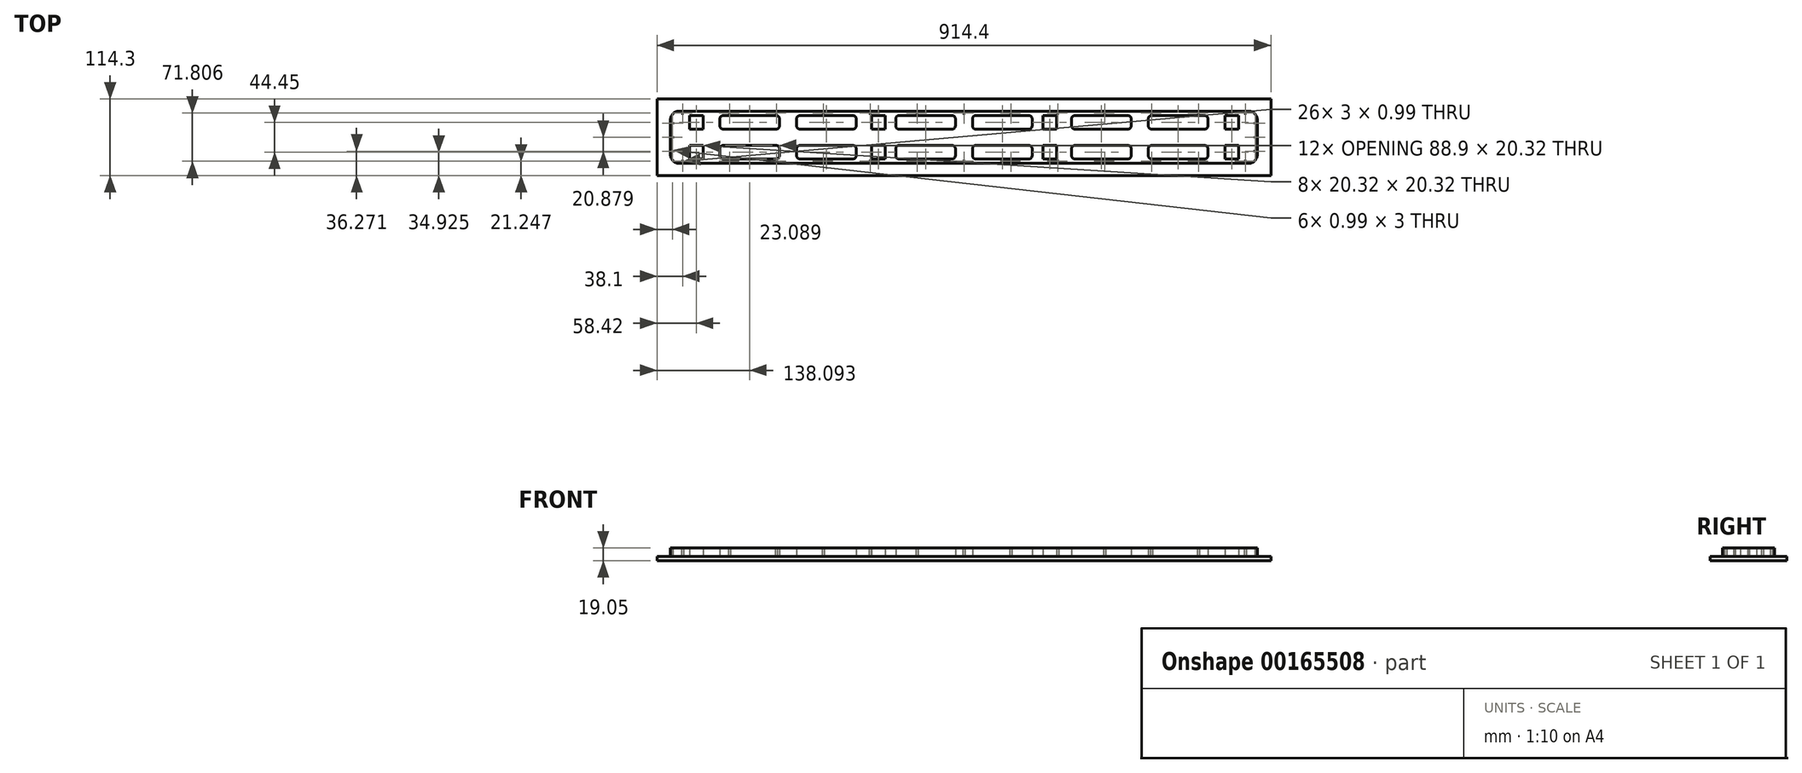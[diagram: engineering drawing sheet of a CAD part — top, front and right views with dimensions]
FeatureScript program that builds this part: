
annotation { "Feature Type Name" : "Feature", "Feature Type Description" : "" }
export const myFeature = defineFeature(function(context is Context, id is Id, definition is map)
    precondition{}
    {
        {
            var Q0;
            Q0=qCreatedBy(makeId("Top.planeOp"),FACE);
            var sketch = newSketch(context, id + "F0", { "sketchPlane" : qUnion([Q0])});
            skLineSegment(sketch, "E0.bottom", {"start": v(137.8, 12.06) * mm, "end": v(117.48, 12.06) * mm});
            skLineSegment(sketch, "E0.top", {"start": v(137.8, 32.39) * mm, "end": v(117.48, 32.39) * mm});
            skLineSegment(sketch, "E0.left", {"start": v(137.8, 12.07) * mm, "end": v(137.8, 32.38) * mm});
            skLineSegment(sketch, "E0.right", {"start": v(117.48, 12.07) * mm, "end": v(117.48, 32.38) * mm});
            skPoint(sketch, "E0.middle", {"position": v(127.64, 22.23) * mm});
            skLineSegment(sketch, "E1.bottom", {"start": v(-437, 38.79) * mm, "end": v(437, 38.79) * mm});
            skLineSegment(sketch, "E1.top", {"start": v(-437, -38.79) * mm, "end": v(437, -38.79) * mm});
            skLineSegment(sketch, "E1.left", {"start": v(-437, 38.79) * mm, "end": v(-437, -38.79) * mm});
            skLineSegment(sketch, "E1.right", {"start": v(437, 38.79) * mm, "end": v(437, -38.79) * mm});
            skPoint(sketch, "E1.middle", {"position": v(0, 0) * mm});
            skLineSegment(sketch, "E2.bottom", {"start": v(457.2, -57.15) * mm, "end": v(-457.2, -57.15) * mm, "construction": true});
            skLineSegment(sketch, "E2.top", {"start": v(457.2, 57.15) * mm, "end": v(-457.2, 57.15) * mm, "construction": true});
            skLineSegment(sketch, "E2.left", {"start": v(457.2, -57.15) * mm, "end": v(457.2, 57.15) * mm, "construction": true});
            skLineSegment(sketch, "E2.right", {"start": v(-457.2, -57.15) * mm, "end": v(-457.2, 57.15) * mm, "construction": true});
            skLineSegment(sketch, "E3.bottom", {"start": v(1.5, 35.4) * mm, "end": v(-1.5, 35.4) * mm});
            skLineSegment(sketch, "E3.top", {"start": v(1.5, 36.4) * mm, "end": v(-1.5, 36.4) * mm});
            skLineSegment(sketch, "E3.left", {"start": v(1.5, 35.4) * mm, "end": v(1.5, 36.4) * mm});
            skLineSegment(sketch, "E3.right", {"start": v(-1.5, 35.4) * mm, "end": v(-1.5, 36.4) * mm});
            skPoint(sketch, "E3.middle", {"position": v(0, 35.9) * mm});
            skLineSegment(sketch, "E4", {"start": v(127.64, 32.39) * mm, "end": v(127.64, 38.79) * mm, "construction": true});
            skLineSegment(sketch, "E5.1.0.0", {"start": v(71.35, 36.4) * mm, "end": v(68.35, 36.4) * mm});
            skLineSegment(sketch, "E5.1.0.1", {"start": v(68.35, 35.4) * mm, "end": v(68.35, 36.4) * mm});
            skLineSegment(sketch, "E5.1.0.2", {"start": v(71.35, 35.4) * mm, "end": v(68.35, 35.4) * mm});
            skLineSegment(sketch, "E5.1.0.3", {"start": v(71.35, 35.4) * mm, "end": v(71.35, 36.4) * mm});
            skLineSegment(sketch, "E5.2.0.0", {"start": v(141.2, 36.4) * mm, "end": v(138.2, 36.4) * mm});
            skLineSegment(sketch, "E5.2.0.1", {"start": v(138.2, 35.4) * mm, "end": v(138.2, 36.4) * mm});
            skLineSegment(sketch, "E5.2.0.2", {"start": v(141.2, 35.4) * mm, "end": v(138.2, 35.4) * mm});
            skLineSegment(sketch, "E5.2.0.3", {"start": v(141.2, 35.4) * mm, "end": v(141.2, 36.4) * mm});
            skLineSegment(sketch, "E5.3.0.0", {"start": v(211.05, 36.4) * mm, "end": v(208.05, 36.4) * mm});
            skLineSegment(sketch, "E5.3.0.1", {"start": v(208.05, 35.4) * mm, "end": v(208.05, 36.4) * mm});
            skLineSegment(sketch, "E5.3.0.2", {"start": v(211.05, 35.4) * mm, "end": v(208.05, 35.4) * mm});
            skLineSegment(sketch, "E5.3.0.3", {"start": v(211.05, 35.4) * mm, "end": v(211.05, 36.4) * mm});
            skLineSegment(sketch, "E5.4.0.0", {"start": v(280.9, 36.4) * mm, "end": v(277.9, 36.4) * mm});
            skLineSegment(sketch, "E5.4.0.1", {"start": v(277.9, 35.4) * mm, "end": v(277.9, 36.4) * mm});
            skLineSegment(sketch, "E5.4.0.2", {"start": v(280.9, 35.4) * mm, "end": v(277.9, 35.4) * mm});
            skLineSegment(sketch, "E5.4.0.3", {"start": v(280.9, 35.4) * mm, "end": v(280.9, 36.4) * mm});
            skLineSegment(sketch, "E5.5.0.0", {"start": v(350.75, 36.4) * mm, "end": v(347.75, 36.4) * mm});
            skLineSegment(sketch, "E5.5.0.1", {"start": v(347.75, 35.4) * mm, "end": v(347.75, 36.4) * mm});
            skLineSegment(sketch, "E5.5.0.2", {"start": v(350.75, 35.4) * mm, "end": v(347.75, 35.4) * mm});
            skLineSegment(sketch, "E5.5.0.3", {"start": v(350.75, 35.4) * mm, "end": v(350.75, 36.4) * mm});
            skLineSegment(sketch, "E5.6.0.0", {"start": v(420.6, 36.4) * mm, "end": v(417.6, 36.4) * mm});
            skLineSegment(sketch, "E5.6.0.1", {"start": v(417.6, 35.4) * mm, "end": v(417.6, 36.4) * mm});
            skLineSegment(sketch, "E5.6.0.2", {"start": v(420.6, 35.4) * mm, "end": v(417.6, 35.4) * mm});
            skLineSegment(sketch, "E5.6.0.3", {"start": v(420.6, 35.4) * mm, "end": v(420.6, 36.4) * mm});
            skLineSegment(sketch, "E5.direction1", {"start": v(-1.5, 36.4) * mm, "end": v(68.35, 36.4) * mm, "construction": true});
            skLineSegment(sketch, "E6.MirrorCS", {"start": v(-138.2, 35.4) * mm, "end": v(-138.2, 36.4) * mm});
            skLineSegment(sketch, "E7.MirrorCS", {"start": v(-141.2, 36.4) * mm, "end": v(-138.2, 36.4) * mm});
            skLineSegment(sketch, "E8.MirrorCS", {"start": v(-420.6, 36.4) * mm, "end": v(-417.6, 36.4) * mm});
            skLineSegment(sketch, "E9.MirrorCS", {"start": v(-280.9, 35.4) * mm, "end": v(-280.9, 36.4) * mm});
            skLineSegment(sketch, "E10.MirrorCS", {"start": v(-280.9, 35.4) * mm, "end": v(-277.9, 35.4) * mm});
            skLineSegment(sketch, "E11.MirrorCS", {"start": v(-277.9, 35.4) * mm, "end": v(-277.9, 36.4) * mm});
            skLineSegment(sketch, "E12.MirrorCS", {"start": v(-280.9, 36.4) * mm, "end": v(-277.9, 36.4) * mm});
            skLineSegment(sketch, "E13.MirrorCS", {"start": v(-141.2, 35.4) * mm, "end": v(-141.2, 36.4) * mm});
            skLineSegment(sketch, "E14.MirrorCS", {"start": v(-420.6, 35.4) * mm, "end": v(-420.6, 36.4) * mm});
            skLineSegment(sketch, "E15.MirrorCS", {"start": v(-141.2, 35.4) * mm, "end": v(-138.2, 35.4) * mm});
            skLineSegment(sketch, "E16.MirrorCS", {"start": v(-420.6, 35.4) * mm, "end": v(-417.6, 35.4) * mm});
            skLineSegment(sketch, "E17.MirrorCS", {"start": v(-71.35, 35.4) * mm, "end": v(-71.35, 36.4) * mm});
            skLineSegment(sketch, "E18.MirrorCS", {"start": v(-350.75, 35.4) * mm, "end": v(-350.75, 36.4) * mm});
            skLineSegment(sketch, "E19.MirrorCS", {"start": v(-71.35, 35.4) * mm, "end": v(-68.35, 35.4) * mm});
            skLineSegment(sketch, "E20.MirrorCS", {"start": v(-350.75, 35.4) * mm, "end": v(-347.75, 35.4) * mm});
            skLineSegment(sketch, "E21.MirrorCS", {"start": v(-68.35, 35.4) * mm, "end": v(-68.35, 36.4) * mm});
            skLineSegment(sketch, "E22.MirrorCS", {"start": v(-347.75, 35.4) * mm, "end": v(-347.75, 36.4) * mm});
            skLineSegment(sketch, "E23.MirrorCS", {"start": v(-71.35, 36.4) * mm, "end": v(-68.35, 36.4) * mm});
            skLineSegment(sketch, "E24.MirrorCS", {"start": v(-350.75, 36.4) * mm, "end": v(-347.75, 36.4) * mm});
            skLineSegment(sketch, "E25.MirrorCS", {"start": v(-211.05, 35.4) * mm, "end": v(-211.05, 36.4) * mm});
            skLineSegment(sketch, "E26.MirrorCS", {"start": v(-211.05, 35.4) * mm, "end": v(-208.05, 35.4) * mm});
            skLineSegment(sketch, "E27.MirrorCS", {"start": v(-211.05, 36.4) * mm, "end": v(-208.05, 36.4) * mm});
            skLineSegment(sketch, "E28.MirrorCS", {"start": v(-417.6, 35.4) * mm, "end": v(-417.6, 36.4) * mm});
            skLineSegment(sketch, "E29.MirrorCS", {"start": v(-208.05, 35.4) * mm, "end": v(-208.05, 36.4) * mm});
            skLineSegment(sketch, "E30.MirrorCS", {"start": v(71.35, -36.4) * mm, "end": v(68.35, -36.4) * mm});
            skLineSegment(sketch, "E31.MirrorCS", {"start": v(1.5, -36.4) * mm, "end": v(-1.5, -36.4) * mm});
            skLineSegment(sketch, "E32.MirrorCS", {"start": v(1.5, -35.4) * mm, "end": v(-1.5, -35.4) * mm});
            skLineSegment(sketch, "E33.MirrorCS", {"start": v(141.2, -35.4) * mm, "end": v(138.2, -35.4) * mm});
            skLineSegment(sketch, "E34.MirrorCS", {"start": v(138.2, -35.4) * mm, "end": v(138.2, -36.4) * mm});
            skLineSegment(sketch, "E35.MirrorCS", {"start": v(141.2, -36.4) * mm, "end": v(138.2, -36.4) * mm});
            skLineSegment(sketch, "E36.MirrorCS", {"start": v(71.35, -35.4) * mm, "end": v(71.35, -36.4) * mm});
            skLineSegment(sketch, "E37.MirrorCS", {"start": v(71.35, -35.4) * mm, "end": v(68.35, -35.4) * mm});
            skLineSegment(sketch, "E38.MirrorCS", {"start": v(68.35, -35.4) * mm, "end": v(68.35, -36.4) * mm});
            skLineSegment(sketch, "E39.MirrorCS", {"start": v(350.75, -36.4) * mm, "end": v(347.75, -36.4) * mm});
            skLineSegment(sketch, "E40.MirrorCS", {"start": v(-1.5, -35.4) * mm, "end": v(-1.5, -36.4) * mm});
            skLineSegment(sketch, "E41.MirrorCS", {"start": v(1.5, -35.4) * mm, "end": v(1.5, -36.4) * mm});
            skLineSegment(sketch, "E42.MirrorCS", {"start": v(-71.35, -35.4) * mm, "end": v(-68.35, -35.4) * mm});
            skLineSegment(sketch, "E43.MirrorCS", {"start": v(-420.6, -36.4) * mm, "end": v(-417.6, -36.4) * mm});
            skLineSegment(sketch, "E44.MirrorCS", {"start": v(141.2, -35.4) * mm, "end": v(141.2, -36.4) * mm});
            skLineSegment(sketch, "E45.MirrorCS", {"start": v(211.05, -36.4) * mm, "end": v(208.05, -36.4) * mm});
            skLineSegment(sketch, "E46.MirrorCS", {"start": v(-280.9, -35.4) * mm, "end": v(-280.9, -36.4) * mm});
            skLineSegment(sketch, "E47.MirrorCS", {"start": v(-211.05, -35.4) * mm, "end": v(-211.05, -36.4) * mm});
            skLineSegment(sketch, "E48.MirrorCS", {"start": v(-138.2, -35.4) * mm, "end": v(-138.2, -36.4) * mm});
            skLineSegment(sketch, "E49.MirrorCS", {"start": v(-350.75, -35.4) * mm, "end": v(-347.75, -35.4) * mm});
            skLineSegment(sketch, "E50.MirrorCS", {"start": v(420.6, -35.4) * mm, "end": v(417.6, -35.4) * mm});
            skLineSegment(sketch, "E51.MirrorCS", {"start": v(280.9, -36.4) * mm, "end": v(277.9, -36.4) * mm});
            skLineSegment(sketch, "E52.MirrorCS", {"start": v(417.6, -35.4) * mm, "end": v(417.6, -36.4) * mm});
            skLineSegment(sketch, "E53.MirrorCS", {"start": v(-350.75, -35.4) * mm, "end": v(-350.75, -36.4) * mm});
            skLineSegment(sketch, "E54.MirrorCS", {"start": v(420.6, -36.4) * mm, "end": v(417.6, -36.4) * mm});
            skLineSegment(sketch, "E55.MirrorCS", {"start": v(-71.35, -35.4) * mm, "end": v(-71.35, -36.4) * mm});
            skLineSegment(sketch, "E56.MirrorCS", {"start": v(350.75, -35.4) * mm, "end": v(350.75, -36.4) * mm});
            skLineSegment(sketch, "E57.MirrorCS", {"start": v(-420.6, -35.4) * mm, "end": v(-417.6, -35.4) * mm});
            skLineSegment(sketch, "E58.MirrorCS", {"start": v(350.75, -35.4) * mm, "end": v(347.75, -35.4) * mm});
            skLineSegment(sketch, "E59.MirrorCS", {"start": v(-141.2, -35.4) * mm, "end": v(-138.2, -35.4) * mm});
            skLineSegment(sketch, "E60.MirrorCS", {"start": v(347.75, -35.4) * mm, "end": v(347.75, -36.4) * mm});
            skLineSegment(sketch, "E61.MirrorCS", {"start": v(-420.6, -35.4) * mm, "end": v(-420.6, -36.4) * mm});
            skLineSegment(sketch, "E62.MirrorCS", {"start": v(-280.9, -36.4) * mm, "end": v(-277.9, -36.4) * mm});
            skLineSegment(sketch, "E63.MirrorCS", {"start": v(-417.6, -35.4) * mm, "end": v(-417.6, -36.4) * mm});
            skLineSegment(sketch, "E64.MirrorCS", {"start": v(280.9, -35.4) * mm, "end": v(280.9, -36.4) * mm});
            skLineSegment(sketch, "E65.MirrorCS", {"start": v(-208.05, -35.4) * mm, "end": v(-208.05, -36.4) * mm});
            skLineSegment(sketch, "E66.MirrorCS", {"start": v(-141.2, -35.4) * mm, "end": v(-141.2, -36.4) * mm});
            skLineSegment(sketch, "E67.MirrorCS", {"start": v(-277.9, -35.4) * mm, "end": v(-277.9, -36.4) * mm});
            skLineSegment(sketch, "E68.MirrorCS", {"start": v(-211.05, -36.4) * mm, "end": v(-208.05, -36.4) * mm});
            skLineSegment(sketch, "E69.MirrorCS", {"start": v(280.9, -35.4) * mm, "end": v(277.9, -35.4) * mm});
            skLineSegment(sketch, "E70.MirrorCS", {"start": v(-280.9, -35.4) * mm, "end": v(-277.9, -35.4) * mm});
            skLineSegment(sketch, "E71.MirrorCS", {"start": v(-211.05, -35.4) * mm, "end": v(-208.05, -35.4) * mm});
            skLineSegment(sketch, "E72.MirrorCS", {"start": v(277.9, -35.4) * mm, "end": v(277.9, -36.4) * mm});
            skLineSegment(sketch, "E73.MirrorCS", {"start": v(-350.75, -36.4) * mm, "end": v(-347.75, -36.4) * mm});
            skLineSegment(sketch, "E74.MirrorCS", {"start": v(211.05, -35.4) * mm, "end": v(211.05, -36.4) * mm});
            skLineSegment(sketch, "E75.MirrorCS", {"start": v(-68.35, -35.4) * mm, "end": v(-68.35, -36.4) * mm});
            skLineSegment(sketch, "E76.MirrorCS", {"start": v(208.05, -35.4) * mm, "end": v(208.05, -36.4) * mm});
            skLineSegment(sketch, "E77.MirrorCS", {"start": v(-347.75, -35.4) * mm, "end": v(-347.75, -36.4) * mm});
            skLineSegment(sketch, "E78.MirrorCS", {"start": v(211.05, -35.4) * mm, "end": v(208.05, -35.4) * mm});
            skLineSegment(sketch, "E79.MirrorCS", {"start": v(420.6, -35.4) * mm, "end": v(420.6, -36.4) * mm});
            skLineSegment(sketch, "E80.MirrorCS", {"start": v(-141.2, -36.4) * mm, "end": v(-138.2, -36.4) * mm});
            skLineSegment(sketch, "E81.MirrorCS", {"start": v(-71.35, -36.4) * mm, "end": v(-68.35, -36.4) * mm});
            skLineSegment(sketch, "E82.MirrorCS", {"start": v(-1.5, -36.4) * mm, "end": v(68.35, -36.4) * mm, "construction": true});
            skLineSegment(sketch, "E83.bottom", {"start": v(434.6, -1.5) * mm, "end": v(433.62, -1.5) * mm});
            skLineSegment(sketch, "E83.top", {"start": v(434.6, 1.5) * mm, "end": v(433.62, 1.5) * mm});
            skLineSegment(sketch, "E83.left", {"start": v(434.6, -1.5) * mm, "end": v(434.6, 1.5) * mm});
            skLineSegment(sketch, "E83.right", {"start": v(433.62, -1.5) * mm, "end": v(433.62, 1.5) * mm});
            skPoint(sketch, "E83.middle", {"position": v(434.11, 0) * mm});
            skPoint(sketch, "E84", {"position": v(437, 0) * mm});
            skLineSegment(sketch, "E85.bottom", {"start": v(433.62, 19.38) * mm, "end": v(434.6, 19.38) * mm});
            skLineSegment(sketch, "E85.top", {"start": v(433.62, 22.38) * mm, "end": v(434.6, 22.38) * mm});
            skLineSegment(sketch, "E85.left", {"start": v(433.62, 19.38) * mm, "end": v(433.62, 22.38) * mm});
            skLineSegment(sketch, "E85.right", {"start": v(434.6, 19.38) * mm, "end": v(434.6, 22.38) * mm});
            skPoint(sketch, "E85.middle", {"position": v(434.11, 20.88) * mm});
            skLineSegment(sketch, "E86.MirrorCS", {"start": v(433.62, -19.38) * mm, "end": v(434.6, -19.38) * mm});
            skLineSegment(sketch, "E87.MirrorCS", {"start": v(433.62, -22.38) * mm, "end": v(434.6, -22.38) * mm});
            skLineSegment(sketch, "E88.MirrorCS", {"start": v(433.62, -19.38) * mm, "end": v(433.62, -22.38) * mm});
            skPoint(sketch, "E89.MirrorP", {"position": v(434.11, -20.88) * mm});
            skLineSegment(sketch, "E90.MirrorCS", {"start": v(434.6, -19.38) * mm, "end": v(434.6, -22.38) * mm});
            skLineSegment(sketch, "E91.MirrorCS", {"start": v(-433.62, -22.38) * mm, "end": v(-434.6, -22.38) * mm});
            skLineSegment(sketch, "E92.MirrorCS", {"start": v(-433.62, 19.38) * mm, "end": v(-434.6, 19.38) * mm});
            skLineSegment(sketch, "E93.MirrorCS", {"start": v(-434.6, 1.5) * mm, "end": v(-433.62, 1.5) * mm});
            skLineSegment(sketch, "E94.MirrorCS", {"start": v(-434.6, -1.5) * mm, "end": v(-433.62, -1.5) * mm});
            skLineSegment(sketch, "E95.MirrorCS", {"start": v(-433.62, -19.38) * mm, "end": v(-434.6, -19.38) * mm});
            skLineSegment(sketch, "E96.MirrorCS", {"start": v(-433.62, 22.38) * mm, "end": v(-434.6, 22.38) * mm});
            skLineSegment(sketch, "E97.MirrorCS", {"start": v(-434.6, 19.38) * mm, "end": v(-434.6, 22.38) * mm});
            skLineSegment(sketch, "E98.MirrorCS", {"start": v(-433.62, 19.38) * mm, "end": v(-433.62, 22.38) * mm});
            skLineSegment(sketch, "E99.MirrorCS", {"start": v(-433.62, -1.5) * mm, "end": v(-433.62, 1.5) * mm});
            skLineSegment(sketch, "E100.MirrorCS", {"start": v(-434.6, -19.38) * mm, "end": v(-434.6, -22.38) * mm});
            skLineSegment(sketch, "E101.MirrorCS", {"start": v(-434.6, -1.5) * mm, "end": v(-434.6, 1.5) * mm});
            skLineSegment(sketch, "E102.MirrorCS", {"start": v(-433.62, -19.38) * mm, "end": v(-433.62, -22.38) * mm});
            skPoint(sketch, "E103.MirrorP", {"position": v(-434.11, -20.88) * mm});
            skPoint(sketch, "E104.MirrorP", {"position": v(-437, 0) * mm});
            skPoint(sketch, "E105.MirrorP", {"position": v(-434.11, 20.88) * mm});
            skPoint(sketch, "E106.MirrorP", {"position": v(-434.11, 0) * mm});
            skLineSegment(sketch, "E107.bottom", {"start": v(12.7, 12.07) * mm, "end": v(101.6, 12.07) * mm});
            skLineSegment(sketch, "E107.top", {"start": v(12.7, 32.39) * mm, "end": v(101.6, 32.39) * mm});
            skLineSegment(sketch, "E107.right", {"start": v(101.6, 12.07) * mm, "end": v(101.6, 32.39) * mm});
            skLineSegment(sketch, "E108", {"start": v(127.64, 22.23) * mm, "end": v(396.28, 22.23) * mm, "construction": true});
            skLineSegment(sketch, "E109.bottom", {"start": v(408.94, 12.07) * mm, "end": v(388.62, 12.07) * mm});
            skLineSegment(sketch, "E109.top", {"start": v(408.94, 32.39) * mm, "end": v(388.62, 32.39) * mm});
            skLineSegment(sketch, "E109.left", {"start": v(408.94, 12.07) * mm, "end": v(408.94, 32.39) * mm});
            skLineSegment(sketch, "E109.right", {"start": v(388.62, 12.07) * mm, "end": v(388.62, 32.39) * mm});
            skPoint(sketch, "E109.middle", {"position": v(398.78, 22.23) * mm});
            skLineSegment(sketch, "E110.bottom", {"start": v(160.36, 12.06) * mm, "end": v(249.26, 12.06) * mm});
            skLineSegment(sketch, "E110.top", {"start": v(160.36, 32.39) * mm, "end": v(249.26, 32.39) * mm});
            skLineSegment(sketch, "E110.left", {"start": v(160.36, 12.06) * mm, "end": v(160.36, 32.38) * mm});
            skLineSegment(sketch, "E110.right", {"start": v(363.56, 12.06) * mm, "end": v(363.56, 32.38) * mm});
            skLineSegment(sketch, "E111.MirrorCS", {"start": v(-12.7, 32.39) * mm, "end": v(-101.6, 32.39) * mm});
            skLineSegment(sketch, "E112.MirrorCS", {"start": v(-12.7, 12.07) * mm, "end": v(-101.6, 12.07) * mm});
            skLineSegment(sketch, "E113.MirrorCS", {"start": v(-101.6, 12.07) * mm, "end": v(-101.6, 32.39) * mm});
            skLineSegment(sketch, "E114.MirrorCS", {"start": v(-137.8, 12.07) * mm, "end": v(-137.8, 32.38) * mm});
            skLineSegment(sketch, "E115.MirrorCS", {"start": v(-137.8, 12.06) * mm, "end": v(-117.48, 12.06) * mm});
            skLineSegment(sketch, "E116.MirrorCS", {"start": v(-137.8, 32.39) * mm, "end": v(-117.48, 32.39) * mm});
            skLineSegment(sketch, "E117.MirrorCS", {"start": v(-127.64, 22.23) * mm, "end": v(-396.28, 22.23) * mm, "construction": true});
            skLineSegment(sketch, "E118.MirrorCS", {"start": v(-408.94, 12.07) * mm, "end": v(-388.62, 12.07) * mm});
            skLineSegment(sketch, "E119.MirrorCS", {"start": v(-388.62, 12.07) * mm, "end": v(-388.62, 32.39) * mm});
            skLineSegment(sketch, "E120.MirrorCS", {"start": v(-408.94, 12.07) * mm, "end": v(-408.94, 32.39) * mm});
            skPoint(sketch, "E121.MirrorP", {"position": v(-398.78, 22.23) * mm});
            skLineSegment(sketch, "E122.MirrorCS", {"start": v(-160.36, 12.06) * mm, "end": v(-249.26, 12.06) * mm});
            skPoint(sketch, "E123.MirrorP", {"position": v(-261.96, 22.23) * mm});
            skLineSegment(sketch, "E124.MirrorCS", {"start": v(-160.36, 32.39) * mm, "end": v(-249.26, 32.39) * mm});
            skLineSegment(sketch, "E125.MirrorCS", {"start": v(-160.36, 12.06) * mm, "end": v(-160.36, 32.38) * mm});
            skPoint(sketch, "E126.MirrorP", {"position": v(-127.64, 22.23) * mm});
            skLineSegment(sketch, "E127.MirrorCS", {"start": v(-363.56, 12.06) * mm, "end": v(-363.56, 32.38) * mm});
            skLineSegment(sketch, "E128.MirrorCS", {"start": v(-408.94, 32.39) * mm, "end": v(-388.62, 32.39) * mm});
            skLineSegment(sketch, "E129.MirrorCS", {"start": v(-117.48, 12.07) * mm, "end": v(-117.48, 32.38) * mm});
            skLineSegment(sketch, "E130", {"start": v(0, 32.39) * mm, "end": v(0, 12.07) * mm, "construction": true});
            skLineSegment(sketch, "E131.MirrorCS", {"start": v(0, -32.39) * mm, "end": v(0, -12.07) * mm, "construction": true});
            skLineSegment(sketch, "E132.MirrorCS", {"start": v(101.6, -12.07) * mm, "end": v(101.6, -32.39) * mm});
            skLineSegment(sketch, "E133.MirrorCS", {"start": v(-160.36, -12.06) * mm, "end": v(-249.26, -12.06) * mm});
            skLineSegment(sketch, "E134.MirrorCS", {"start": v(-12.7, -12.07) * mm, "end": v(-101.6, -12.07) * mm});
            skLineSegment(sketch, "E135.MirrorCS", {"start": v(-160.36, -12.07) * mm, "end": v(-160.36, -32.38) * mm});
            skPoint(sketch, "E136.MirrorP", {"position": v(-127.64, -22.23) * mm});
            skLineSegment(sketch, "E137.MirrorCS", {"start": v(12.7, -32.39) * mm, "end": v(101.6, -32.39) * mm});
            skLineSegment(sketch, "E138.MirrorCS", {"start": v(408.94, -12.07) * mm, "end": v(388.62, -12.07) * mm});
            skLineSegment(sketch, "E139.MirrorCS", {"start": v(388.62, -12.07) * mm, "end": v(388.62, -32.39) * mm});
            skLineSegment(sketch, "E140.MirrorCS", {"start": v(-363.56, -12.07) * mm, "end": v(-363.56, -32.38) * mm});
            skLineSegment(sketch, "E141.MirrorCS", {"start": v(160.36, -32.39) * mm, "end": v(249.26, -32.39) * mm});
            skLineSegment(sketch, "E142.MirrorCS", {"start": v(-117.48, -12.07) * mm, "end": v(-117.48, -32.38) * mm});
            skLineSegment(sketch, "E143.MirrorCS", {"start": v(127.64, -22.23) * mm, "end": v(396.28, -22.23) * mm, "construction": true});
            skLineSegment(sketch, "E144.MirrorCS", {"start": v(363.56, -12.07) * mm, "end": v(363.56, -32.38) * mm});
            skLineSegment(sketch, "E145.MirrorCS", {"start": v(160.36, -12.06) * mm, "end": v(249.26, -12.06) * mm});
            skLineSegment(sketch, "E146.MirrorCS", {"start": v(-408.94, -32.39) * mm, "end": v(-388.62, -32.39) * mm});
            skLineSegment(sketch, "E147.MirrorCS", {"start": v(160.36, -12.07) * mm, "end": v(160.36, -32.38) * mm});
            skLineSegment(sketch, "E148.MirrorCS", {"start": v(-160.36, -32.39) * mm, "end": v(-249.26, -32.39) * mm});
            skLineSegment(sketch, "E149.MirrorCS", {"start": v(-101.6, -12.07) * mm, "end": v(-101.6, -32.39) * mm});
            skPoint(sketch, "E150.MirrorP", {"position": v(0, -35.9) * mm});
            skPoint(sketch, "E151.MirrorP", {"position": v(127.64, -22.23) * mm});
            skLineSegment(sketch, "E152.MirrorCS", {"start": v(-12.7, -32.39) * mm, "end": v(-101.6, -32.39) * mm});
            skLineSegment(sketch, "E153.MirrorCS", {"start": v(408.94, -12.07) * mm, "end": v(408.94, -32.39) * mm});
            skLineSegment(sketch, "E154.MirrorCS", {"start": v(-408.94, -12.07) * mm, "end": v(-408.94, -32.39) * mm});
            skLineSegment(sketch, "E155.MirrorCS", {"start": v(408.94, -32.39) * mm, "end": v(388.62, -32.39) * mm});
            skLineSegment(sketch, "E156.MirrorCS", {"start": v(-137.8, -12.07) * mm, "end": v(-137.8, -32.38) * mm});
            skLineSegment(sketch, "E157.MirrorCS", {"start": v(-137.8, -12.06) * mm, "end": v(-117.48, -12.06) * mm});
            skLineSegment(sketch, "E158.MirrorCS", {"start": v(-127.64, -22.23) * mm, "end": v(-396.28, -22.23) * mm, "construction": true});
            skLineSegment(sketch, "E159.MirrorCS", {"start": v(-137.8, -32.39) * mm, "end": v(-117.48, -32.39) * mm});
            skLineSegment(sketch, "E160.MirrorCS", {"start": v(-408.94, -12.07) * mm, "end": v(-388.62, -12.07) * mm});
            skLineSegment(sketch, "E161.MirrorCS", {"start": v(137.8, -12.06) * mm, "end": v(117.48, -12.06) * mm});
            skLineSegment(sketch, "E162.MirrorCS", {"start": v(137.8, -12.07) * mm, "end": v(137.8, -32.38) * mm});
            skLineSegment(sketch, "E163.MirrorCS", {"start": v(137.8, -32.39) * mm, "end": v(117.48, -32.39) * mm});
            skLineSegment(sketch, "E164.MirrorCS", {"start": v(117.48, -12.07) * mm, "end": v(117.48, -32.38) * mm});
            skPoint(sketch, "E165.MirrorP", {"position": v(398.78, -22.23) * mm});
            skPoint(sketch, "E166.MirrorP", {"position": v(-398.78, -22.23) * mm});
            skLineSegment(sketch, "E167.MirrorCS", {"start": v(-388.62, -12.07) * mm, "end": v(-388.62, -32.39) * mm});
            skLineSegment(sketch, "E168.MirrorCS", {"start": v(12.7, -12.07) * mm, "end": v(101.6, -12.07) * mm});
            skPoint(sketch, "E169.MirrorP", {"position": v(-261.96, -22.23) * mm});
            skLineSegment(sketch, "E170", {"start": v(12.7, 32.39) * mm, "end": v(12.7, 12.07) * mm});
            skLineSegment(sketch, "E171.MirrorCS", {"start": v(-12.7, 32.39) * mm, "end": v(-12.7, 12.07) * mm});
            skPoint(sketch, "E172.orphan", {"position": v(0, 32.39) * mm});
            skPoint(sketch, "E173.orphan", {"position": v(0, 12.07) * mm});
            skLineSegment(sketch, "E174.left", {"start": v(274.66, 12.06) * mm, "end": v(274.66, 32.38) * mm});
            skLineSegment(sketch, "E174.right", {"start": v(249.26, 12.06) * mm, "end": v(249.26, 32.39) * mm});
            skLineSegment(sketch, "E175.trimOffspring", {"start": v(274.66, 32.39) * mm, "end": v(363.56, 32.39) * mm});
            skLineSegment(sketch, "E176.trimOffspring", {"start": v(274.66, 12.06) * mm, "end": v(363.56, 12.06) * mm});
            skLineSegment(sketch, "E177.MirrorCS", {"start": v(-249.26, 12.06) * mm, "end": v(-249.26, 32.39) * mm});
            skLineSegment(sketch, "E178.MirrorCS", {"start": v(-274.66, 12.06) * mm, "end": v(-274.66, 32.38) * mm});
            skLineSegment(sketch, "E179.MirrorCS", {"start": v(249.26, -12.06) * mm, "end": v(249.26, -32.39) * mm});
            skLineSegment(sketch, "E180.MirrorCS", {"start": v(274.66, -12.06) * mm, "end": v(274.66, -32.38) * mm});
            skLineSegment(sketch, "E181.MirrorCS", {"start": v(12.7, -32.39) * mm, "end": v(12.7, -12.07) * mm});
            skLineSegment(sketch, "E182.MirrorCS", {"start": v(-12.7, -32.39) * mm, "end": v(-12.7, -12.07) * mm});
            skLineSegment(sketch, "E183.MirrorCS", {"start": v(-249.26, -12.06) * mm, "end": v(-249.26, -32.39) * mm});
            skLineSegment(sketch, "E184.MirrorCS", {"start": v(-274.66, -12.06) * mm, "end": v(-274.66, -32.38) * mm});
            skLineSegment(sketch, "E185.trimOffspring", {"start": v(274.66, -12.06) * mm, "end": v(363.56, -12.06) * mm});
            skLineSegment(sketch, "E186.trimOffspring", {"start": v(274.66, -32.39) * mm, "end": v(363.56, -32.39) * mm});
            skLineSegment(sketch, "E187.trimOffspring", {"start": v(-274.66, -12.06) * mm, "end": v(-363.56, -12.06) * mm});
            skLineSegment(sketch, "E188.trimOffspring", {"start": v(-274.66, -32.39) * mm, "end": v(-363.56, -32.39) * mm});
            skLineSegment(sketch, "E189.trimOffspring", {"start": v(-274.66, 12.06) * mm, "end": v(-363.56, 12.06) * mm});
            skLineSegment(sketch, "E190.trimOffspring", {"start": v(-274.66, 32.39) * mm, "end": v(-363.56, 32.39) * mm});
            skPoint(sketch, "E191.orphan", {"position": v(0, -12.07) * mm});
            skPoint(sketch, "E192.orphan", {"position": v(0, -32.39) * mm});
            skSolve(sketch);
        }
        {
            var Q0;
            Q0=qSketchRegion(id+"F0",true);
            extrude(context, id + "F1", {"entities" : qUnion([Q0]), "depth" : 12.7 * mm});
        }
        {
            var Q0;
            Q0=makeQuery(id+"F1.opExtrude","CAP_FACE",FACE,{"disambiguationData":[OSD([sQuery(id+"F0.wireOp",EDGE,"E0.bottom"),sQuery(id+"F0.wireOp",EDGE,"E0.top"),sQuery(id+"F0.wireOp",EDGE,"E0.left"),sQuery(id+"F0.wireOp",EDGE,"E0.right"),sQuery(id+"F0.wireOp",EDGE,"c7728689-f15c-40d8-94a0-aa7cfa5ef08a0.MirrorCS"),sQuery(id+"F0.wireOp",EDGE,"c7728689-f15c-40d8-94a0-aa7cfa5ef08a2.MirrorCS"),sQuery(id+"F0.wireOp",EDGE,"c7728689-f15c-40d8-94a0-aa7cfa5ef08a3.MirrorCS"),sQuery(id+"F0.wireOp",EDGE,"c7728689-f15c-40d8-94a0-aa7cfa5ef08a4.MirrorCS"),sQuery(id+"F0.wireOp",EDGE,"4dc9d5bf-a38a-4a1e-950f-32d8b5cff3080.MirrorCS"),sQuery(id+"F0.wireOp",EDGE,"4dc9d5bf-a38a-4a1e-950f-32d8b5cff3081.MirrorCS"),sQuery(id+"F0.wireOp",EDGE,"4dc9d5bf-a38a-4a1e-950f-32d8b5cff3083.MirrorCS"),sQuery(id+"F0.wireOp",EDGE,"4dc9d5bf-a38a-4a1e-950f-32d8b5cff3084.MirrorCS"),sQuery(id+"F0.wireOp",EDGE,"4dc9d5bf-a38a-4a1e-950f-32d8b5cff3085.MirrorCS"),sQuery(id+"F0.wireOp",EDGE,"4dc9d5bf-a38a-4a1e-950f-32d8b5cff3086.MirrorCS"),sQuery(id+"F0.wireOp",EDGE,"4dc9d5bf-a38a-4a1e-950f-32d8b5cff3087.MirrorCS"),sQuery(id+"F0.wireOp",EDGE,"4dc9d5bf-a38a-4a1e-950f-32d8b5cff3089.MirrorCS"),sQuery(id+"F0.wireOp",EDGE,"Djwg6WnG-kNIB-h8U3-zt6q-135kBUQRGHdk.bottom"),sQuery(id+"F0.wireOp",EDGE,"Djwg6WnG-kNIB-h8U3-zt6q-135kBUQRGHdk.top"),sQuery(id+"F0.wireOp",EDGE,"Djwg6WnG-kNIB-h8U3-zt6q-135kBUQRGHdk.left"),sQuery(id+"F0.wireOp",EDGE,"Djwg6WnG-kNIB-h8U3-zt6q-135kBUQRGHdk.right"),sQuery(id+"F0.wireOp",EDGE,"16b2a2c5-597f-43df-b698-45636335e0a50.MirrorCS"),sQuery(id+"F0.wireOp",EDGE,"16b2a2c5-597f-43df-b698-45636335e0a51.MirrorCS"),sQuery(id+"F0.wireOp",EDGE,"16b2a2c5-597f-43df-b698-45636335e0a53.MirrorCS"),sQuery(id+"F0.wireOp",EDGE,"16b2a2c5-597f-43df-b698-45636335e0a54.MirrorCS"),sQuery(id+"F0.wireOp",EDGE,"c691ba4f-4d1f-4ff7-9d60-ffc56f4ab8f80.MirrorCS"),sQuery(id+"F0.wireOp",EDGE,"c691ba4f-4d1f-4ff7-9d60-ffc56f4ab8f81.MirrorCS"),sQuery(id+"F0.wireOp",EDGE,"c691ba4f-4d1f-4ff7-9d60-ffc56f4ab8f82.MirrorCS"),sQuery(id+"F0.wireOp",EDGE,"c691ba4f-4d1f-4ff7-9d60-ffc56f4ab8f84.MirrorCS"),sQuery(id+"F0.wireOp",EDGE,"3abc38f9-7f5c-417c-b53a-6495ec21e5f80.MirrorCS"),sQuery(id+"F0.wireOp",EDGE,"3abc38f9-7f5c-417c-b53a-6495ec21e5f81.MirrorCS"),sQuery(id+"F0.wireOp",EDGE,"3abc38f9-7f5c-417c-b53a-6495ec21e5f82.MirrorCS"),sQuery(id+"F0.wireOp",EDGE,"3abc38f9-7f5c-417c-b53a-6495ec21e5f84.MirrorCS"),sQuery(id+"F0.wireOp",EDGE,"E1.bottom"),sQuery(id+"F0.wireOp",EDGE,"E1.top"),sQuery(id+"F0.wireOp",EDGE,"E1.left"),sQuery(id+"F0.wireOp",EDGE,"E1.right")])],"isStart":true});
            var sketch = newSketch(context, id + "F2", { "sketchPlane" : qUnion([Q0])});
            skLineSegment(sketch, "E193.bottom", {"start": v(457.2, -57.15) * mm, "end": v(-457.2, -57.15) * mm});
            skLineSegment(sketch, "E193.top", {"start": v(457.2, 57.15) * mm, "end": v(-457.2, 57.15) * mm});
            skLineSegment(sketch, "E193.left", {"start": v(457.2, -57.15) * mm, "end": v(457.2, 57.15) * mm});
            skLineSegment(sketch, "E193.right", {"start": v(-457.2, -57.15) * mm, "end": v(-457.2, 57.15) * mm});
            skPoint(sketch, "E193.middle", {"position": v(0, 0) * mm});
            skSolve(sketch);
        }
        {
            var Q0;
            Q0=qSketchRegion(id+"F2",true);
            extrude(context, id + "F3", {"entities" : qUnion([Q0]), "depth" : 6.35 * mm});
        }
        {
            var Q0;
            Q0=makeQuery(id+"F1.opExtrude","SWEPT_EDGE",EDGE,{"disambiguationData":[OSD([sQuery(id+"F0.wireOp",EDGE,"E1.bottom"),sQuery(id+"F0.wireOp",EDGE,"E1.left")])]});
            var Q1;
            Q1=makeQuery(id+"F1.opExtrude","SWEPT_EDGE",EDGE,{"disambiguationData":[OSD([sQuery(id+"F0.wireOp",EDGE,"E1.top"),sQuery(id+"F0.wireOp",EDGE,"E1.left")])]});
            var Q2;
            Q2=makeQuery(id+"F1.opExtrude","SWEPT_EDGE",EDGE,{"disambiguationData":[OSD([sQuery(id+"F0.wireOp",EDGE,"E1.bottom"),sQuery(id+"F0.wireOp",EDGE,"E1.right")])]});
            var Q3;
            Q3=makeQuery(id+"F1.opExtrude","SWEPT_EDGE",EDGE,{"disambiguationData":[OSD([sQuery(id+"F0.wireOp",EDGE,"E1.top"),sQuery(id+"F0.wireOp",EDGE,"E1.right")])]});
            fillet(context, id + "F4", {"entities" : qUnion([Q0, Q1, Q2, Q3]), "radius" : 12.7 * mm, "tangentPropagation" : true, "allowEdgeOverflow" : false});
        }
        {
            var Q0;
            Q0=makeQuery(id+"F1.opExtrude","SWEPT_EDGE",EDGE,{"disambiguationData":[OSD([sQuery(id+"F0.wireOp",EDGE,"E144.MirrorCS"),sQuery(id+"F0.wireOp",EDGE,"E185.trimOffspring")])]});
            var Q1;
            Q1=makeQuery(id+"F1.opExtrude","SWEPT_EDGE",EDGE,{"disambiguationData":[OSD([sQuery(id+"F0.wireOp",EDGE,"E145.MirrorCS"),sQuery(id+"F0.wireOp",EDGE,"E179.MirrorCS")])]});
            var Q2;
            Q2=makeQuery(id+"F1.opExtrude","SWEPT_EDGE",EDGE,{"disambiguationData":[OSD([sQuery(id+"F0.wireOp",EDGE,"E110.top"),sQuery(id+"F0.wireOp",EDGE,"E174.right")])]});
            var Q3;
            Q3=makeQuery(id+"F1.opExtrude","SWEPT_EDGE",EDGE,{"disambiguationData":[OSD([sQuery(id+"F0.wireOp",EDGE,"E110.right"),sQuery(id+"F0.wireOp",EDGE,"E175.trimOffspring")])]});
            var Q4;
            Q4=makeQuery(id+"F1.opExtrude","SWEPT_EDGE",EDGE,{"disambiguationData":[OSD([sQuery(id+"F0.wireOp",EDGE,"E132.MirrorCS"),sQuery(id+"F0.wireOp",EDGE,"E168.MirrorCS")])]});
            var Q5;
            Q5=makeQuery(id+"F1.opExtrude","SWEPT_EDGE",EDGE,{"disambiguationData":[OSD([sQuery(id+"F0.wireOp",EDGE,"E107.top"),sQuery(id+"F0.wireOp",EDGE,"E107.right")])]});
            var Q6;
            Q6=makeQuery(id+"F1.opExtrude","SWEPT_EDGE",EDGE,{"disambiguationData":[OSD([sQuery(id+"F0.wireOp",EDGE,"E134.MirrorCS"),sQuery(id+"F0.wireOp",EDGE,"E182.MirrorCS")])]});
            var Q7;
            Q7=makeQuery(id+"F1.opExtrude","SWEPT_EDGE",EDGE,{"disambiguationData":[OSD([sQuery(id+"F0.wireOp",EDGE,"E111.MirrorCS"),sQuery(id+"F0.wireOp",EDGE,"E171.MirrorCS")])]});
            var Q8;
            Q8=makeQuery(id+"F1.opExtrude","SWEPT_EDGE",EDGE,{"disambiguationData":[OSD([sQuery(id+"F0.wireOp",EDGE,"E133.MirrorCS"),sQuery(id+"F0.wireOp",EDGE,"E135.MirrorCS")])]});
            var Q9;
            Q9=makeQuery(id+"F1.opExtrude","SWEPT_EDGE",EDGE,{"disambiguationData":[OSD([sQuery(id+"F0.wireOp",EDGE,"E124.MirrorCS"),sQuery(id+"F0.wireOp",EDGE,"E125.MirrorCS")])]});
            var Q10;
            Q10=makeQuery(id+"F1.opExtrude","SWEPT_EDGE",EDGE,{"disambiguationData":[OSD([sQuery(id+"F0.wireOp",EDGE,"E178.MirrorCS"),sQuery(id+"F0.wireOp",EDGE,"E190.trimOffspring")])]});
            var Q11;
            Q11=makeQuery(id+"F1.opExtrude","SWEPT_EDGE",EDGE,{"disambiguationData":[OSD([sQuery(id+"F0.wireOp",EDGE,"E184.MirrorCS"),sQuery(id+"F0.wireOp",EDGE,"E187.trimOffspring")])]});
            var Q12;
            Q12=makeQuery(id+"F1.opExtrude","SWEPT_EDGE",EDGE,{"disambiguationData":[OSD([sQuery(id+"F0.wireOp",EDGE,"E140.MirrorCS"),sQuery(id+"F0.wireOp",EDGE,"E188.trimOffspring")])]});
            var Q13;
            Q13=makeQuery(id+"F1.opExtrude","SWEPT_EDGE",EDGE,{"disambiguationData":[OSD([sQuery(id+"F0.wireOp",EDGE,"E127.MirrorCS"),sQuery(id+"F0.wireOp",EDGE,"E189.trimOffspring")])]});
            var Q14;
            Q14=makeQuery(id+"F1.opExtrude","SWEPT_EDGE",EDGE,{"disambiguationData":[OSD([sQuery(id+"F0.wireOp",EDGE,"E122.MirrorCS"),sQuery(id+"F0.wireOp",EDGE,"E177.MirrorCS")])]});
            var Q15;
            Q15=makeQuery(id+"F1.opExtrude","SWEPT_EDGE",EDGE,{"disambiguationData":[OSD([sQuery(id+"F0.wireOp",EDGE,"E148.MirrorCS"),sQuery(id+"F0.wireOp",EDGE,"E183.MirrorCS")])]});
            var Q16;
            Q16=makeQuery(id+"F1.opExtrude","SWEPT_EDGE",EDGE,{"disambiguationData":[OSD([sQuery(id+"F0.wireOp",EDGE,"E112.MirrorCS"),sQuery(id+"F0.wireOp",EDGE,"E113.MirrorCS")])]});
            var Q17;
            Q17=makeQuery(id+"F1.opExtrude","SWEPT_EDGE",EDGE,{"disambiguationData":[OSD([sQuery(id+"F0.wireOp",EDGE,"E149.MirrorCS"),sQuery(id+"F0.wireOp",EDGE,"E152.MirrorCS")])]});
            var Q18;
            Q18=makeQuery(id+"F1.opExtrude","SWEPT_EDGE",EDGE,{"disambiguationData":[OSD([sQuery(id+"F0.wireOp",EDGE,"E141.MirrorCS"),sQuery(id+"F0.wireOp",EDGE,"E147.MirrorCS")])]});
            var Q19;
            Q19=makeQuery(id+"F1.opExtrude","SWEPT_EDGE",EDGE,{"disambiguationData":[OSD([sQuery(id+"F0.wireOp",EDGE,"E137.MirrorCS"),sQuery(id+"F0.wireOp",EDGE,"E181.MirrorCS")])]});
            var Q20;
            Q20=makeQuery(id+"F1.opExtrude","SWEPT_EDGE",EDGE,{"disambiguationData":[OSD([sQuery(id+"F0.wireOp",EDGE,"E107.top"),sQuery(id+"F0.wireOp",EDGE,"E170")])]});
            var Q21;
            Q21=makeQuery(id+"F1.opExtrude","SWEPT_EDGE",EDGE,{"disambiguationData":[OSD([sQuery(id+"F0.wireOp",EDGE,"E111.MirrorCS"),sQuery(id+"F0.wireOp",EDGE,"E113.MirrorCS")])]});
            var Q22;
            Q22=makeQuery(id+"F1.opExtrude","SWEPT_EDGE",EDGE,{"disambiguationData":[OSD([sQuery(id+"F0.wireOp",EDGE,"E124.MirrorCS"),sQuery(id+"F0.wireOp",EDGE,"E177.MirrorCS")])]});
            var Q23;
            Q23=makeQuery(id+"F1.opExtrude","SWEPT_EDGE",EDGE,{"disambiguationData":[OSD([sQuery(id+"F0.wireOp",EDGE,"E133.MirrorCS"),sQuery(id+"F0.wireOp",EDGE,"E183.MirrorCS")])]});
            var Q24;
            Q24=makeQuery(id+"F1.opExtrude","SWEPT_EDGE",EDGE,{"disambiguationData":[OSD([sQuery(id+"F0.wireOp",EDGE,"E140.MirrorCS"),sQuery(id+"F0.wireOp",EDGE,"E187.trimOffspring")])]});
            var Q25;
            Q25=makeQuery(id+"F1.opExtrude","SWEPT_EDGE",EDGE,{"disambiguationData":[OSD([sQuery(id+"F0.wireOp",EDGE,"E127.MirrorCS"),sQuery(id+"F0.wireOp",EDGE,"E190.trimOffspring")])]});
            var Q26;
            Q26=makeQuery(id+"F1.opExtrude","SWEPT_EDGE",EDGE,{"disambiguationData":[OSD([sQuery(id+"F0.wireOp",EDGE,"E122.MirrorCS"),sQuery(id+"F0.wireOp",EDGE,"E125.MirrorCS")])]});
            var Q27;
            Q27=makeQuery(id+"F1.opExtrude","SWEPT_EDGE",EDGE,{"disambiguationData":[OSD([sQuery(id+"F0.wireOp",EDGE,"E152.MirrorCS"),sQuery(id+"F0.wireOp",EDGE,"E182.MirrorCS")])]});
            var Q28;
            Q28=makeQuery(id+"F1.opExtrude","SWEPT_EDGE",EDGE,{"disambiguationData":[OSD([sQuery(id+"F0.wireOp",EDGE,"E112.MirrorCS"),sQuery(id+"F0.wireOp",EDGE,"E171.MirrorCS")])]});
            var Q29;
            Q29=makeQuery(id+"F1.opExtrude","SWEPT_EDGE",EDGE,{"disambiguationData":[OSD([sQuery(id+"F0.wireOp",EDGE,"E145.MirrorCS"),sQuery(id+"F0.wireOp",EDGE,"E147.MirrorCS")])]});
            var Q30;
            Q30=makeQuery(id+"F1.opExtrude","SWEPT_EDGE",EDGE,{"disambiguationData":[OSD([sQuery(id+"F0.wireOp",EDGE,"E168.MirrorCS"),sQuery(id+"F0.wireOp",EDGE,"E181.MirrorCS")])]});
            var Q31;
            Q31=makeQuery(id+"F1.opExtrude","SWEPT_EDGE",EDGE,{"disambiguationData":[OSD([sQuery(id+"F0.wireOp",EDGE,"E134.MirrorCS"),sQuery(id+"F0.wireOp",EDGE,"E149.MirrorCS")])]});
            var Q32;
            Q32=makeQuery(id+"F1.opExtrude","SWEPT_EDGE",EDGE,{"disambiguationData":[OSD([sQuery(id+"F0.wireOp",EDGE,"E180.MirrorCS"),sQuery(id+"F0.wireOp",EDGE,"E185.trimOffspring")])]});
            var Q33;
            Q33=makeQuery(id+"F1.opExtrude","SWEPT_EDGE",EDGE,{"disambiguationData":[OSD([sQuery(id+"F0.wireOp",EDGE,"E174.left"),sQuery(id+"F0.wireOp",EDGE,"E175.trimOffspring")])]});
            var Q34;
            Q34=makeQuery(id+"F1.opExtrude","SWEPT_EDGE",EDGE,{"disambiguationData":[OSD([sQuery(id+"F0.wireOp",EDGE,"E110.top"),sQuery(id+"F0.wireOp",EDGE,"E110.left")])]});
            var Q35;
            Q35=makeQuery(id+"F1.opExtrude","SWEPT_EDGE",EDGE,{"disambiguationData":[OSD([sQuery(id+"F0.wireOp",EDGE,"E110.right"),sQuery(id+"F0.wireOp",EDGE,"E176.trimOffspring")])]});
            var Q36;
            Q36=makeQuery(id+"F1.opExtrude","SWEPT_EDGE",EDGE,{"disambiguationData":[OSD([sQuery(id+"F0.wireOp",EDGE,"E144.MirrorCS"),sQuery(id+"F0.wireOp",EDGE,"E186.trimOffspring")])]});
            var Q37;
            Q37=makeQuery(id+"F1.opExtrude","SWEPT_EDGE",EDGE,{"disambiguationData":[OSD([sQuery(id+"F0.wireOp",EDGE,"E141.MirrorCS"),sQuery(id+"F0.wireOp",EDGE,"E179.MirrorCS")])]});
            var Q38;
            Q38=makeQuery(id+"F1.opExtrude","SWEPT_EDGE",EDGE,{"disambiguationData":[OSD([sQuery(id+"F0.wireOp",EDGE,"E110.bottom"),sQuery(id+"F0.wireOp",EDGE,"E174.right")])]});
            var Q39;
            Q39=makeQuery(id+"F1.opExtrude","SWEPT_EDGE",EDGE,{"disambiguationData":[OSD([sQuery(id+"F0.wireOp",EDGE,"E132.MirrorCS"),sQuery(id+"F0.wireOp",EDGE,"E137.MirrorCS")])]});
            var Q40;
            Q40=makeQuery(id+"F1.opExtrude","SWEPT_EDGE",EDGE,{"disambiguationData":[OSD([sQuery(id+"F0.wireOp",EDGE,"E180.MirrorCS"),sQuery(id+"F0.wireOp",EDGE,"E186.trimOffspring")])]});
            var Q41;
            Q41=makeQuery(id+"F1.opExtrude","SWEPT_EDGE",EDGE,{"disambiguationData":[OSD([sQuery(id+"F0.wireOp",EDGE,"E174.left"),sQuery(id+"F0.wireOp",EDGE,"E176.trimOffspring")])]});
            var Q42;
            Q42=makeQuery(id+"F1.opExtrude","SWEPT_EDGE",EDGE,{"disambiguationData":[OSD([sQuery(id+"F0.wireOp",EDGE,"E178.MirrorCS"),sQuery(id+"F0.wireOp",EDGE,"E189.trimOffspring")])]});
            var Q43;
            Q43=makeQuery(id+"F1.opExtrude","SWEPT_EDGE",EDGE,{"disambiguationData":[OSD([sQuery(id+"F0.wireOp",EDGE,"E184.MirrorCS"),sQuery(id+"F0.wireOp",EDGE,"E188.trimOffspring")])]});
            var Q44;
            Q44=makeQuery(id+"F1.opExtrude","SWEPT_EDGE",EDGE,{"disambiguationData":[OSD([sQuery(id+"F0.wireOp",EDGE,"E107.bottom"),sQuery(id+"F0.wireOp",EDGE,"E170")])]});
            var Q45;
            Q45=makeQuery(id+"F1.opExtrude","SWEPT_EDGE",EDGE,{"disambiguationData":[OSD([sQuery(id+"F0.wireOp",EDGE,"E110.bottom"),sQuery(id+"F0.wireOp",EDGE,"E110.left")])]});
            fillet(context, id + "F5", {"entities" : qUnion([Q0, Q1, Q2, Q3, Q4, Q5, Q6, Q7, Q8, Q9, Q10, Q11, Q12, Q13, Q14, Q15, Q16, Q17, Q18, Q19, Q20, Q21, Q22, Q23, Q24, Q25, Q26, Q27, Q28, Q29, Q30, Q31, Q32, Q33, Q34, Q35, Q36, Q37, Q38, Q39, Q40, Q41, Q42, Q43, Q44, Q45]), "radius" : 5.08 * mm, "tangentPropagation" : true, "allowEdgeOverflow" : false});
        }
        {
            var Q0;
            Q0=makeQuery(id+"F1.opExtrude","SWEPT_EDGE",EDGE,{"disambiguationData":[OSD([sQuery(id+"F0.wireOp",EDGE,"E184.MirrorCS"),sQuery(id+"F0.wireOp",EDGE,"E188.trimOffspring")])]});
            var Q1;
            Q1=makeQuery(id+"F1.opExtrude","SWEPT_EDGE",EDGE,{"disambiguationData":[OSD([sQuery(id+"F0.wireOp",EDGE,"E135.MirrorCS"),sQuery(id+"F0.wireOp",EDGE,"E148.MirrorCS")])]});
            var Q2;
            Q2=makeQuery(id+"F1.opExtrude","SWEPT_EDGE",EDGE,{"disambiguationData":[OSD([sQuery(id+"F0.wireOp",EDGE,"E152.MirrorCS"),sQuery(id+"F0.wireOp",EDGE,"E182.MirrorCS")])]});
            var Q3;
            Q3=makeQuery(id+"F1.opExtrude","SWEPT_EDGE",EDGE,{"disambiguationData":[OSD([sQuery(id+"F0.wireOp",EDGE,"E112.MirrorCS"),sQuery(id+"F0.wireOp",EDGE,"E171.MirrorCS")])]});
            var Q4;
            Q4=makeQuery(id+"F1.opExtrude","SWEPT_EDGE",EDGE,{"disambiguationData":[OSD([sQuery(id+"F0.wireOp",EDGE,"E132.MirrorCS"),sQuery(id+"F0.wireOp",EDGE,"E137.MirrorCS")])]});
            var Q5;
            Q5=makeQuery(id+"F1.opExtrude","SWEPT_EDGE",EDGE,{"disambiguationData":[OSD([sQuery(id+"F0.wireOp",EDGE,"E107.bottom"),sQuery(id+"F0.wireOp",EDGE,"E107.right")])]});
            var Q6;
            Q6=makeQuery(id+"F1.opExtrude","SWEPT_EDGE",EDGE,{"disambiguationData":[OSD([sQuery(id+"F0.wireOp",EDGE,"E141.MirrorCS"),sQuery(id+"F0.wireOp",EDGE,"E179.MirrorCS")])]});
            var Q7;
            Q7=makeQuery(id+"F1.opExtrude","SWEPT_EDGE",EDGE,{"disambiguationData":[OSD([sQuery(id+"F0.wireOp",EDGE,"E110.bottom"),sQuery(id+"F0.wireOp",EDGE,"E174.right")])]});
            var Q8;
            Q8=makeQuery(id+"F1.opExtrude","SWEPT_EDGE",EDGE,{"disambiguationData":[OSD([sQuery(id+"F0.wireOp",EDGE,"E144.MirrorCS"),sQuery(id+"F0.wireOp",EDGE,"E186.trimOffspring")])]});
            var Q9;
            Q9=makeQuery(id+"F1.opExtrude","SWEPT_EDGE",EDGE,{"disambiguationData":[OSD([sQuery(id+"F0.wireOp",EDGE,"E110.right"),sQuery(id+"F0.wireOp",EDGE,"E176.trimOffspring")])]});
            fillet(context, id + "F6", {"entities" : qUnion([Q0, Q1, Q2, Q3, Q4, Q5, Q6, Q7, Q8, Q9]), "radius" : 5.08 * mm, "tangentPropagation" : true, "allowEdgeOverflow" : false});
        }
    });
